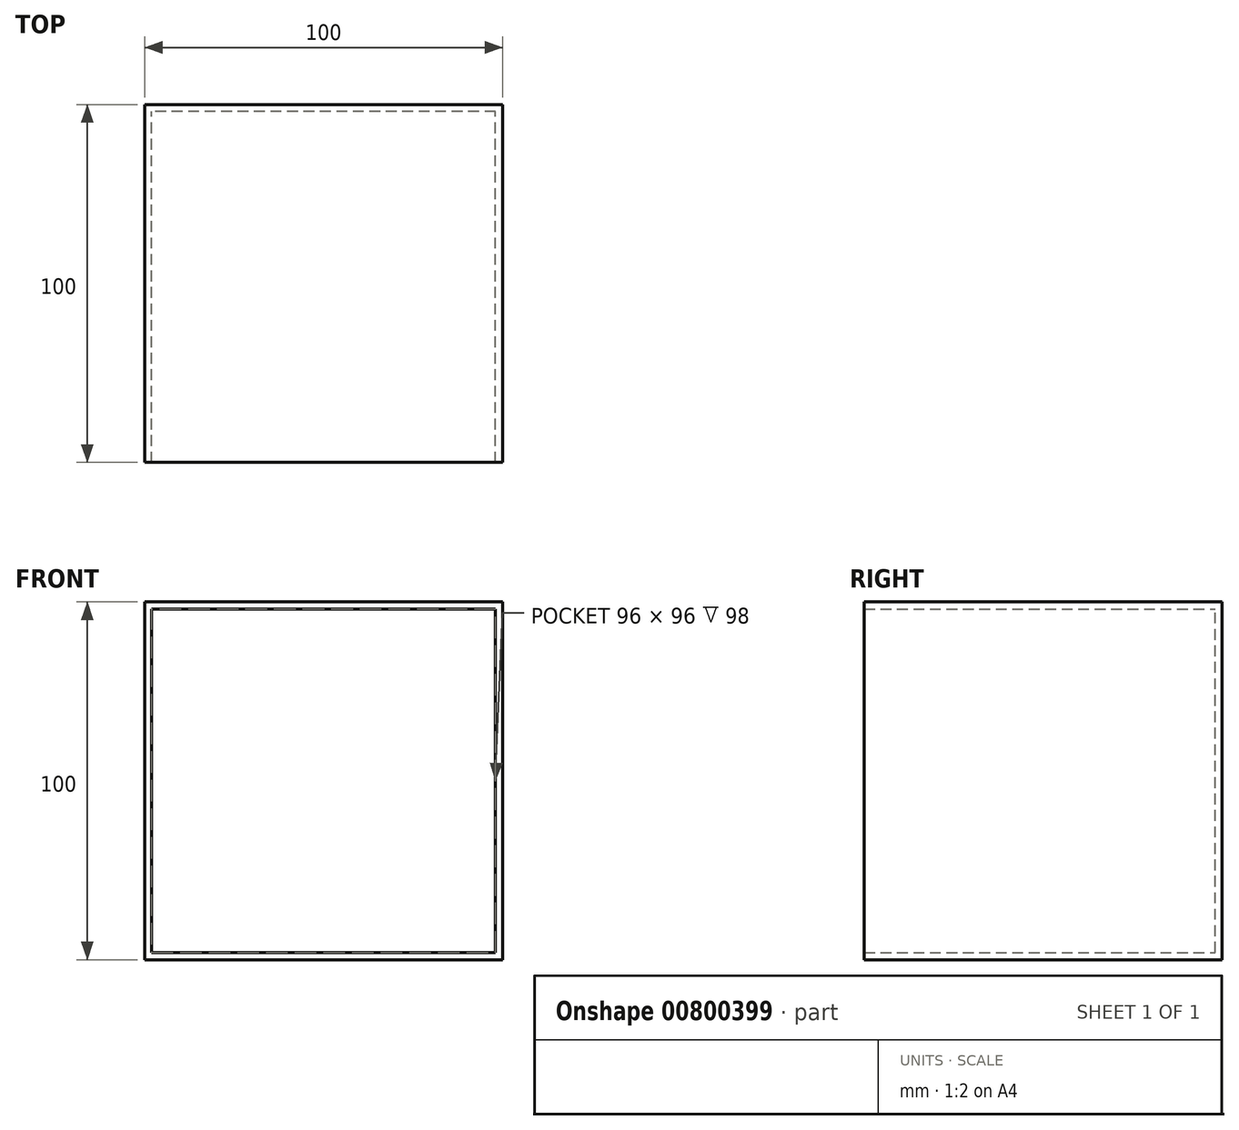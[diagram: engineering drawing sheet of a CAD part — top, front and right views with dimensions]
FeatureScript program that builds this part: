
annotation { "Feature Type Name" : "Feature", "Feature Type Description" : "" }
export const myFeature = defineFeature(function(context is Context, id is Id, definition is map)
    precondition{}
    {
        {
            var Q0;
            Q0=qCreatedBy(makeId("Front.planeOp"),FACE);
            var sketch = newSketch(context, id + "F0", { "sketchPlane" : qUnion([Q0])});
            skLineSegment(sketch, "E0.bottom", {"start": v(50, -50) * mm, "end": v(-50, -50) * mm});
            skLineSegment(sketch, "E0.top", {"start": v(50, 50) * mm, "end": v(-50, 50) * mm});
            skLineSegment(sketch, "E0.left", {"start": v(50, -50) * mm, "end": v(50, 50) * mm});
            skLineSegment(sketch, "E0.right", {"start": v(-50, -50) * mm, "end": v(-50, 50) * mm});
            skPoint(sketch, "E0.middle", {"position": v(0, 0) * mm});
            skLineSegment(sketch, "E1.0", {"start": v(48, -48) * mm, "end": v(-48, -48) * mm});
            skLineSegment(sketch, "E1.1", {"start": v(48, -48) * mm, "end": v(48, 48) * mm});
            skLineSegment(sketch, "E1.2", {"start": v(48, 48) * mm, "end": v(-48, 48) * mm});
            skLineSegment(sketch, "E1.3", {"start": v(-48, -48) * mm, "end": v(-48, 48) * mm});
            skSolve(sketch);
        }
        {
            var Q0;
            Q0=makeQuery(id+"F0.imprint","IMPRINT",FACE,{"disambiguationData":[TD([[makeQuery(id+"F0.imprint","IMPRINT",EDGE,{"derivedFrom":sQuery(id+"F0.wireOp",EDGE,"E1.0")}),-1.0]])]});
            var Q1;
            Q1=sQuery(id+"F0.wireOp",EDGE,"E0.bottom");
            var Q2;
            Q2=sQuery(id+"F0.wireOp",EDGE,"E0.left");
            var Q3;
            Q3=sQuery(id+"F0.wireOp",EDGE,"E0.top");
            var Q4;
            Q4=sQuery(id+"F0.wireOp",EDGE,"E0.right");
            extrude(context, id + "F1", {"entities" : qUnion([Q0]), "surfaceEntities" : qUnion([Q1, Q2, Q3, Q4]), "depth" : 2 * mm, "offsetDistance" : 25 * mm});
        }
        {
            var Q0;
            Q0=makeQuery(id+"F0.imprint","IMPRINT",FACE,{"disambiguationData":[TD([[makeQuery(id+"F0.imprint","IMPRINT",EDGE,{"derivedFrom":sQuery(id+"F0.wireOp",EDGE,"E0.bottom")}),-1.0]])]});
            extrude(context, id + "F2", {"entities" : qUnion([Q0]), "operationType" : NewBodyOperationType.ADD, "depth" : 100 * mm, "offsetDistance" : 25 * mm});
        }
    });
